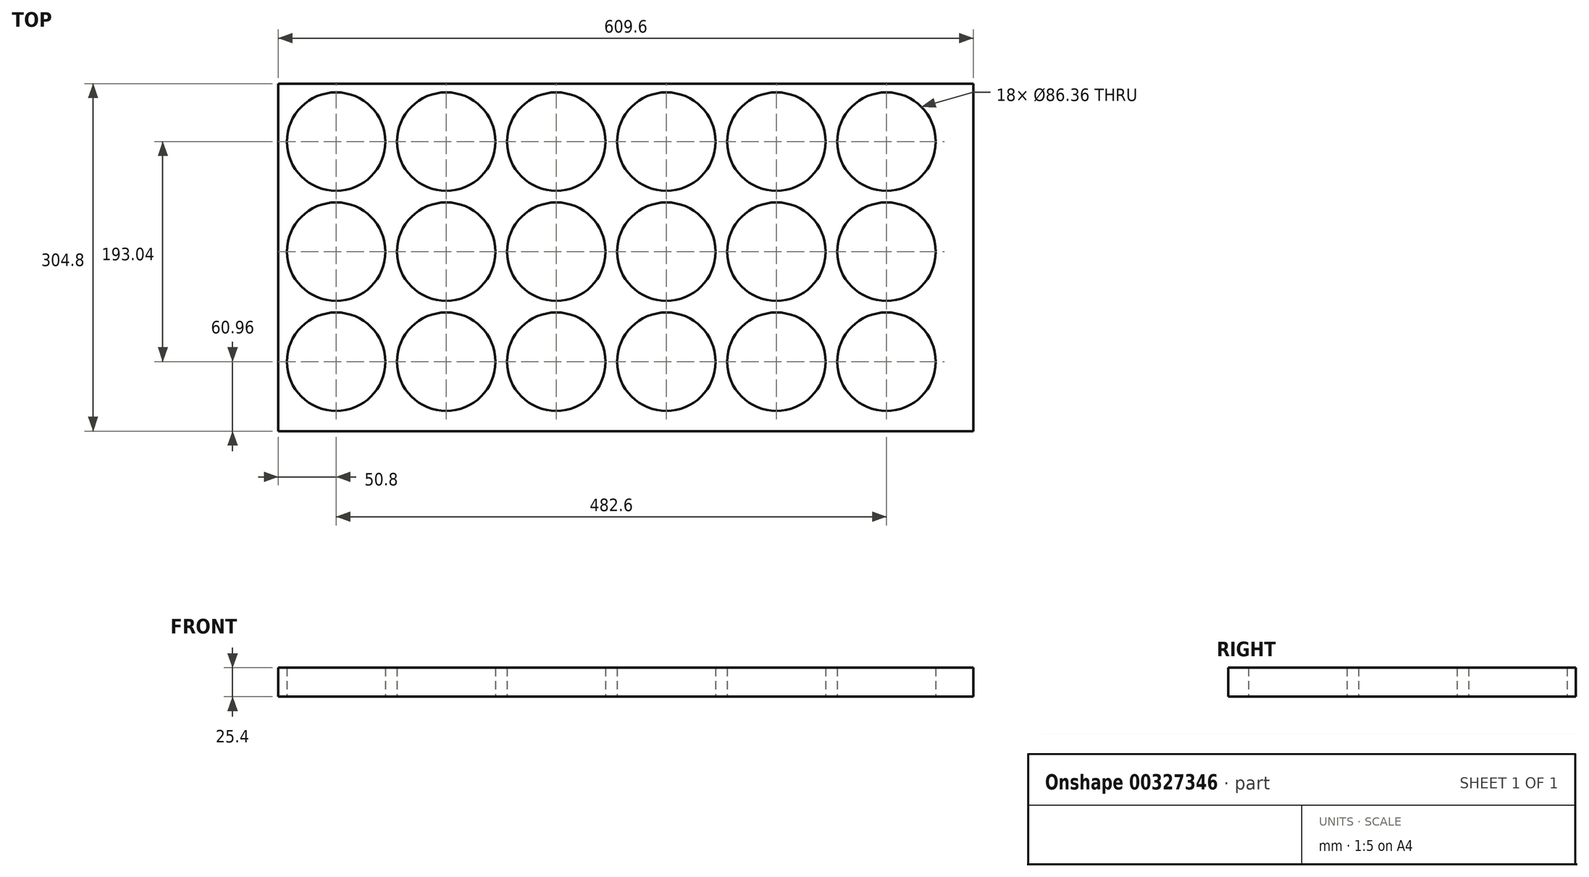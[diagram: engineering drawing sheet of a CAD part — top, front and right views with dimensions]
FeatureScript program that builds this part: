
annotation { "Feature Type Name" : "Feature", "Feature Type Description" : "" }
export const myFeature = defineFeature(function(context is Context, id is Id, definition is map)
    precondition{}
    {
        {
            var Q0;
            Q0=qCreatedBy(makeId("Top.planeOp"),FACE);
            var sketch = newSketch(context, id + "F0", { "sketchPlane" : qUnion([Q0])});
            skLineSegment(sketch, "E0.bottom", {"start": v(304.8, 152.4) * mm, "end": v(-304.8, 152.4) * mm});
            skLineSegment(sketch, "E0.top", {"start": v(304.8, -152.4) * mm, "end": v(-304.8, -152.4) * mm});
            skLineSegment(sketch, "E0.left", {"start": v(304.8, 152.4) * mm, "end": v(304.8, -152.4) * mm});
            skLineSegment(sketch, "E0.right", {"start": v(-304.8, 152.4) * mm, "end": v(-304.8, -152.4) * mm});
            skPoint(sketch, "E0.middle", {"position": v(0, 0) * mm});
            skCircle(sketch, "E1", {"center": v(-254, 101.6) * mm, "radius": 43.18 * mm});
            skCircle(sketch, "E2.0.1.0", {"center": v(-157.48, 101.6) * mm, "radius": 43.18 * mm});
            skCircle(sketch, "E2.0.2.0", {"center": v(-60.96, 101.6) * mm, "radius": 43.18 * mm});
            skCircle(sketch, "E2.0.3.0", {"center": v(35.56, 101.6) * mm, "radius": 43.18 * mm});
            skCircle(sketch, "E2.0.4.0", {"center": v(132.08, 101.6) * mm, "radius": 43.18 * mm});
            skCircle(sketch, "E2.0.5.0", {"center": v(228.6, 101.6) * mm, "radius": 43.18 * mm});
            skCircle(sketch, "E2.1.0.0", {"center": v(-254, 5.08) * mm, "radius": 43.18 * mm});
            skCircle(sketch, "E2.1.1.0", {"center": v(-157.48, 5.08) * mm, "radius": 43.18 * mm});
            skCircle(sketch, "E2.1.2.0", {"center": v(-60.96, 5.08) * mm, "radius": 43.18 * mm});
            skCircle(sketch, "E2.1.3.0", {"center": v(35.56, 5.08) * mm, "radius": 43.18 * mm});
            skCircle(sketch, "E2.1.4.0", {"center": v(132.08, 5.08) * mm, "radius": 43.18 * mm});
            skCircle(sketch, "E2.1.5.0", {"center": v(228.6, 5.08) * mm, "radius": 43.18 * mm});
            skCircle(sketch, "E2.2.0.0", {"center": v(-254, -91.44) * mm, "radius": 43.18 * mm});
            skCircle(sketch, "E2.2.1.0", {"center": v(-157.48, -91.44) * mm, "radius": 43.18 * mm});
            skCircle(sketch, "E2.2.2.0", {"center": v(-60.96, -91.44) * mm, "radius": 43.18 * mm});
            skCircle(sketch, "E2.2.3.0", {"center": v(35.56, -91.44) * mm, "radius": 43.18 * mm});
            skCircle(sketch, "E2.2.4.0", {"center": v(132.08, -91.44) * mm, "radius": 43.18 * mm});
            skCircle(sketch, "E2.2.5.0", {"center": v(228.6, -91.44) * mm, "radius": 43.18 * mm});
            skLineSegment(sketch, "E2.direction1", {"start": v(-254, 101.6) * mm, "end": v(-254, 5.08) * mm, "construction": true});
            skLineSegment(sketch, "E2.direction2", {"start": v(-254, 101.6) * mm, "end": v(-157.48, 101.6) * mm, "construction": true});
            skSolve(sketch);
        }
        {
            var Q0;
            Q0=makeQuery(id+"F0.imprint","IMPRINT",FACE,{"disambiguationData":[TD([[makeQuery(id+"F0.imprint","IMPRINT",EDGE,{"derivedFrom":sQuery(id+"F0.wireOp",EDGE,"E0.bottom")}),1.0]])]});
            extrude(context, id + "F1", {"entities" : qUnion([Q0]), "depth" : 25.4 * mm});
        }
    });
